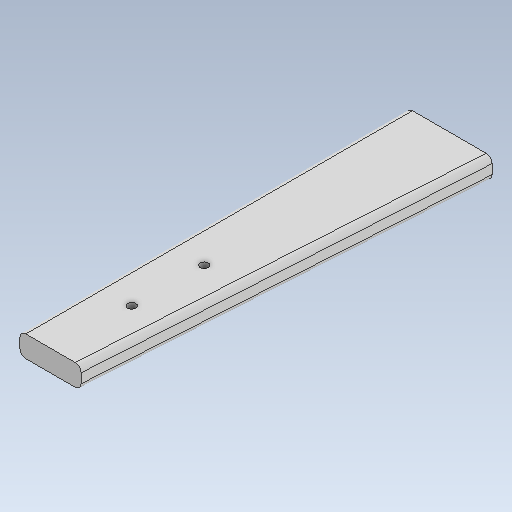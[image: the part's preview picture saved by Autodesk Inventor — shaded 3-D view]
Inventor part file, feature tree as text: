
AUTODESK INVENTOR PART (.ipt)
format: ipt  version: 2020 (Build 240168000, 168)  size: 118,272 bytes
history: native  units: mm
features: sketch x2, extrude x1, hole x1, fillet x1
ambient origin geometry x8: Origin, YZ Plane, XZ Plane, XY Plane, X Axis, Y Axis, Z Axis, Center Point
bodies: Volumenkörper1 (feature_tree)
feature tree (5):
  extrude  "Extrusion1"  Depth=65.0mm
  hole  "Bohrung1"  [1 undecoded]
  fillet  "Rundung1"  Radius=13.0mm
  sketch  "Skizze1"  dims[d0=65.0mm d1=14.4mm]
  sketch  "Skizze2"  dims[d2=10.3mm d3=3.6mm d4=0.0mm d5=13.0mm d6=25.0mm d7=5.8mm d8=6.0mm d9=1.4mm d10=6.0mm d11=4.0mm d12=2.0mm d13=90.0deg d14=8.0mm d15=20.594885mm d16=1.0mm]
note: 1 required parameter value undecoded (feature->parameter linkage not recoverable at this tier; creation-order binding heuristic only, values carry confidence <= 0.55)
